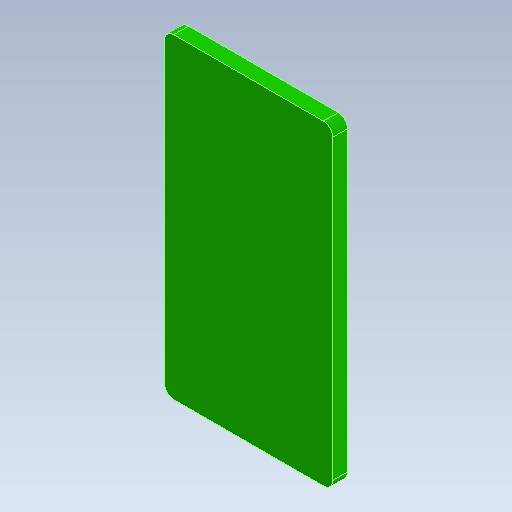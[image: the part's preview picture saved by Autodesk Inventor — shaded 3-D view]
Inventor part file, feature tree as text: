
AUTODESK INVENTOR PART (.ipt)
format: ipt  version: 2021 (Build 250183000, 183)  size: 119,296 bytes
history: native  units: mm
features: extrude x1, fillet x1, other x1, sketch x1, projected_geometry x1
ambient origin geometry x8: Origin, YZ Plane, XZ Plane, XY Plane, X Axis, Y Axis, Z Axis, Center Point
bodies: Solid1 (feature_tree)
feature tree (5):
  extrude  "Extrusion1"  Depth=33.8mm
  fillet  "Fillet1"  Radius=1.6mm
  other  "USB_MAIN_EXTENSION_PCB_OUTLINE"
  sketch  "Sketch1"  dims[d0=18.0mm d1=33.8mm d2=1.6mm d3=0.0mm d4=1.0mm]
  projected_geometry  "Projected Loop1"
